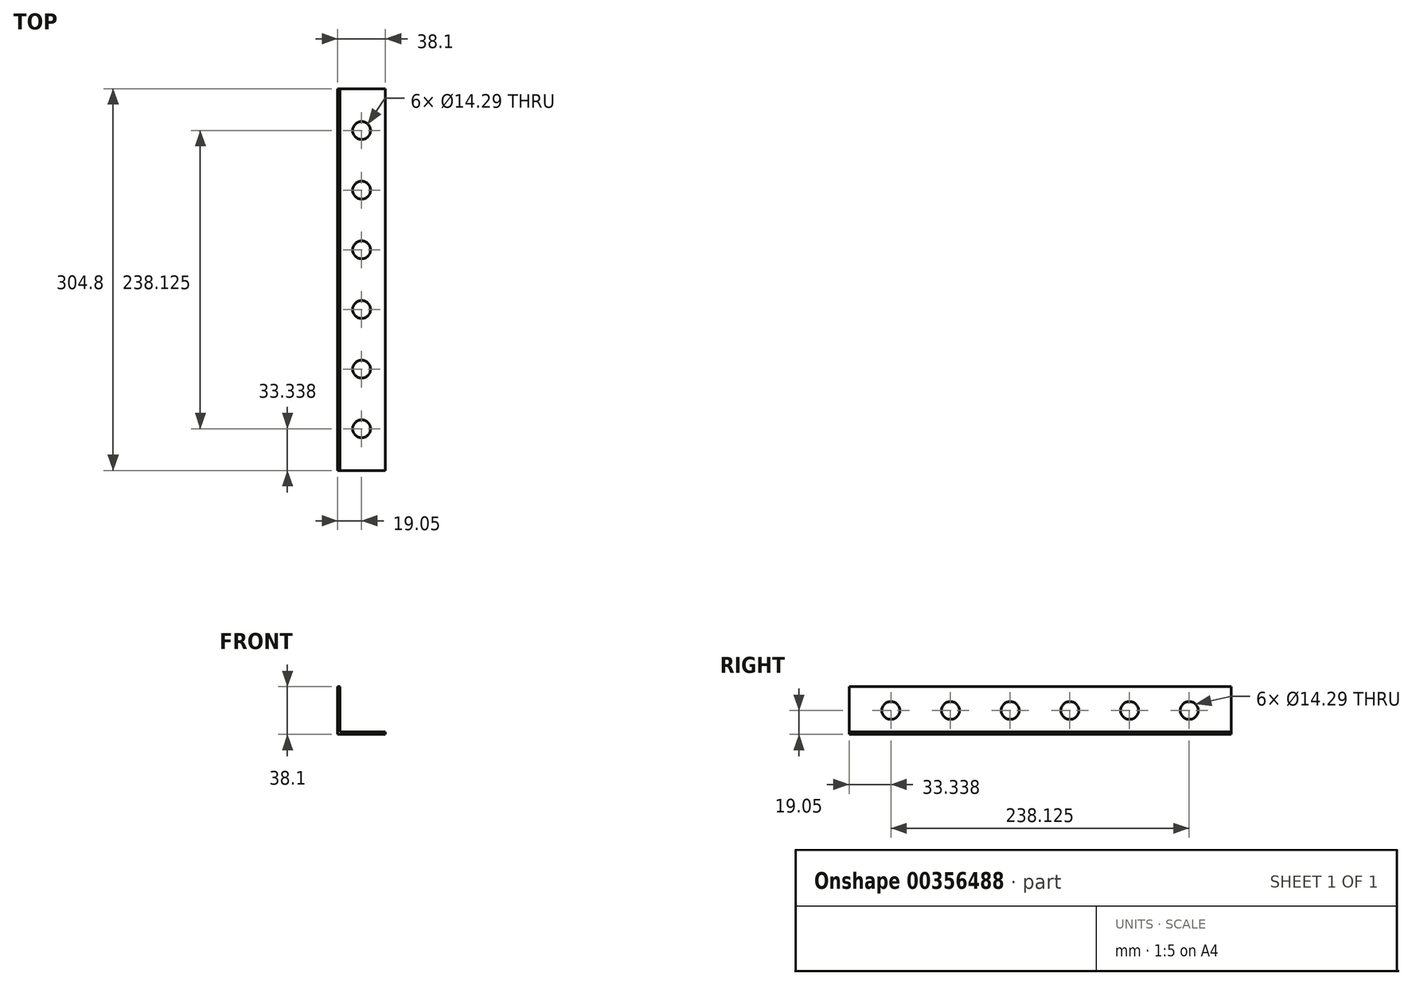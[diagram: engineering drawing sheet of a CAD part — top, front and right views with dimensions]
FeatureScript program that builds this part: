
annotation { "Feature Type Name" : "Feature", "Feature Type Description" : "" }
export const myFeature = defineFeature(function(context is Context, id is Id, definition is map)
    precondition{}
    {
        {
            var Q0;
            Q0=qCreatedBy(makeId("Front.planeOp"),FACE);
            var sketch = newSketch(context, id + "F0", { "sketchPlane" : qUnion([Q0])});
            skLineSegment(sketch, "E0.bottom", {"start": v(0, 0) * mm, "end": v(1.9, 0) * mm});
            skLineSegment(sketch, "E0.top", {"start": v(0, 38.1) * mm, "end": v(1.9, 38.1) * mm});
            skLineSegment(sketch, "E0.left", {"start": v(0, 0) * mm, "end": v(0, 38.1) * mm});
            skLineSegment(sketch, "E0.right", {"start": v(1.9, 0) * mm, "end": v(1.9, 38.1) * mm});
            skLineSegment(sketch, "E1.bottom", {"start": v(1.9, 1.9) * mm, "end": v(38.1, 1.9) * mm});
            skLineSegment(sketch, "E1.top", {"start": v(1.9, 0) * mm, "end": v(38.1, 0) * mm});
            skLineSegment(sketch, "E1.left", {"start": v(1.9, 1.9) * mm, "end": v(1.9, 0) * mm});
            skLineSegment(sketch, "E1.right", {"start": v(38.1, 1.9) * mm, "end": v(38.1, 0) * mm});
            skSolve(sketch);
        }
        {
            var Q0;
            Q0=makeQuery(id+"F0.imprint","IMPRINT",FACE,{"disambiguationData":[TD([[makeQuery(id+"F0.imprint","IMPRINT",EDGE,{"derivedFrom":sQuery(id+"F0.wireOp",EDGE,"E1.bottom")}),-1.0]])]});
            var Q1;
            Q1=makeQuery(id+"F0.imprint","IMPRINT",FACE,{"disambiguationData":[TD([[makeQuery(id+"F0.imprint","IMPRINT",EDGE,{"derivedFrom":sQuery(id+"F0.wireOp",EDGE,"E0.bottom")}),1.0]])]});
            extrude(context, id + "F1", {"entities" : qUnion([Q0, Q1]), "depth" : 304.8 * mm});
        }
        {
            var Q0;
            Q0=makeQuery(id+"F1.opExtrude","SWEPT_FACE",FACE,{"disambiguationData":[OSD([sQuery(id+"F0.wireOp",EDGE,"E1.bottom")])]});
            var sketch = newSketch(context, id + "F2", { "sketchPlane" : qUnion([Q0])});
            skCircle(sketch, "E2", {"center": v(19.05, -271.46) * mm, "radius": 7.14 * mm});
            skCircle(sketch, "E3.0.1.0", {"center": v(19.05, -223.84) * mm, "radius": 7.14 * mm});
            skCircle(sketch, "E3.0.2.0", {"center": v(19.05, -176.21) * mm, "radius": 7.14 * mm});
            skCircle(sketch, "E3.0.3.0", {"center": v(19.05, -128.59) * mm, "radius": 7.14 * mm});
            skCircle(sketch, "E3.0.4.0", {"center": v(19.05, -80.96) * mm, "radius": 7.14 * mm});
            skCircle(sketch, "E3.0.5.0", {"center": v(19.05, -33.34) * mm, "radius": 7.14 * mm});
            skLineSegment(sketch, "E3.direction1", {"start": v(19.05, -292.1) * mm, "end": v(44.45, -292.1) * mm, "construction": true});
            skLineSegment(sketch, "E3.direction2", {"start": v(19.05, -292.1) * mm, "end": v(19.05, -244.48) * mm, "construction": true});
            skSolve(sketch);
        }
        {
            var Q0;
            Q0=makeQuery(id+"F2.imprint","IMPRINT",FACE,{"disambiguationData":[TD([[makeQuery(id+"F2.imprint","IMPRINT",EDGE,{"derivedFrom":sQuery(id+"F2.wireOp",EDGE,"E2")}),1.0]])]});
            var Q1;
            Q1=makeQuery(id+"F2.imprint","IMPRINT",FACE,{"disambiguationData":[TD([[makeQuery(id+"F2.imprint","IMPRINT",EDGE,{"derivedFrom":sQuery(id+"F2.wireOp",EDGE,"E3.0.1.0")}),1.0]])]});
            var Q2;
            Q2=makeQuery(id+"F2.imprint","IMPRINT",FACE,{"disambiguationData":[TD([[makeQuery(id+"F2.imprint","IMPRINT",EDGE,{"derivedFrom":sQuery(id+"F2.wireOp",EDGE,"E3.0.2.0")}),1.0]])]});
            var Q3;
            Q3=makeQuery(id+"F2.imprint","IMPRINT",FACE,{"disambiguationData":[TD([[makeQuery(id+"F2.imprint","IMPRINT",EDGE,{"derivedFrom":sQuery(id+"F2.wireOp",EDGE,"E3.0.3.0")}),1.0]])]});
            var Q4;
            Q4=makeQuery(id+"F2.imprint","IMPRINT",FACE,{"disambiguationData":[TD([[makeQuery(id+"F2.imprint","IMPRINT",EDGE,{"derivedFrom":sQuery(id+"F2.wireOp",EDGE,"E3.0.4.0")}),1.0]])]});
            var Q5;
            Q5=makeQuery(id+"F2.imprint","IMPRINT",FACE,{"disambiguationData":[TD([[makeQuery(id+"F2.imprint","IMPRINT",EDGE,{"derivedFrom":sQuery(id+"F2.wireOp",EDGE,"E3.0.5.0")}),1.0]])]});
            extrude(context, id + "F3", {"entities" : qUnion([Q0, Q1, Q2, Q3, Q4, Q5]), "operationType" : NewBodyOperationType.REMOVE, "oppositeDirection" : true, "depth" : 25.4 * mm});
        }
        {
            var Q0;
            Q0=makeQuery(id+"F1.opExtrude","SWEPT_FACE",FACE,{"disambiguationData":[OSD([sQuery(id+"F0.wireOp",EDGE,"E0.right")])]});
            var sketch = newSketch(context, id + "F4", { "sketchPlane" : qUnion([Q0])});
            skCircle(sketch, "E4", {"center": v(-271.46, 19.05) * mm, "radius": 7.14 * mm});
            skCircle(sketch, "E5.1.0.0", {"center": v(-223.84, 19.05) * mm, "radius": 7.14 * mm});
            skCircle(sketch, "E5.2.0.0", {"center": v(-176.21, 19.05) * mm, "radius": 7.14 * mm});
            skCircle(sketch, "E5.3.0.0", {"center": v(-128.59, 19.05) * mm, "radius": 7.14 * mm});
            skCircle(sketch, "E5.4.0.0", {"center": v(-80.96, 19.05) * mm, "radius": 7.14 * mm});
            skCircle(sketch, "E5.5.0.0", {"center": v(-33.34, 19.05) * mm, "radius": 7.14 * mm});
            skLineSegment(sketch, "E5.direction1", {"start": v(-271.46, 19.05) * mm, "end": v(-223.84, 19.05) * mm, "construction": true});
            skSolve(sketch);
        }
        {
            var Q0;
            Q0=makeQuery(id+"F4.imprint","IMPRINT",FACE,{"disambiguationData":[TD([[makeQuery(id+"F4.imprint","IMPRINT",EDGE,{"derivedFrom":sQuery(id+"F4.wireOp",EDGE,"E4")}),1.0]])]});
            var Q1;
            Q1=makeQuery(id+"F4.imprint","IMPRINT",FACE,{"disambiguationData":[TD([[makeQuery(id+"F4.imprint","IMPRINT",EDGE,{"derivedFrom":sQuery(id+"F4.wireOp",EDGE,"E5.1.0.0")}),1.0]])]});
            var Q2;
            Q2=makeQuery(id+"F4.imprint","IMPRINT",FACE,{"disambiguationData":[TD([[makeQuery(id+"F4.imprint","IMPRINT",EDGE,{"derivedFrom":sQuery(id+"F4.wireOp",EDGE,"E5.2.0.0")}),1.0]])]});
            var Q3;
            Q3=makeQuery(id+"F4.imprint","IMPRINT",FACE,{"disambiguationData":[TD([[makeQuery(id+"F4.imprint","IMPRINT",EDGE,{"derivedFrom":sQuery(id+"F4.wireOp",EDGE,"E5.3.0.0")}),1.0]])]});
            var Q4;
            Q4=makeQuery(id+"F4.imprint","IMPRINT",FACE,{"disambiguationData":[TD([[makeQuery(id+"F4.imprint","IMPRINT",EDGE,{"derivedFrom":sQuery(id+"F4.wireOp",EDGE,"E5.4.0.0")}),1.0]])]});
            var Q5;
            Q5=makeQuery(id+"F4.imprint","IMPRINT",FACE,{"disambiguationData":[TD([[makeQuery(id+"F4.imprint","IMPRINT",EDGE,{"derivedFrom":sQuery(id+"F4.wireOp",EDGE,"E5.5.0.0")}),1.0]])]});
            extrude(context, id + "F5", {"entities" : qUnion([Q0, Q1, Q2, Q3, Q4, Q5]), "operationType" : NewBodyOperationType.REMOVE, "oppositeDirection" : true, "depth" : 25.4 * mm});
        }
    });
